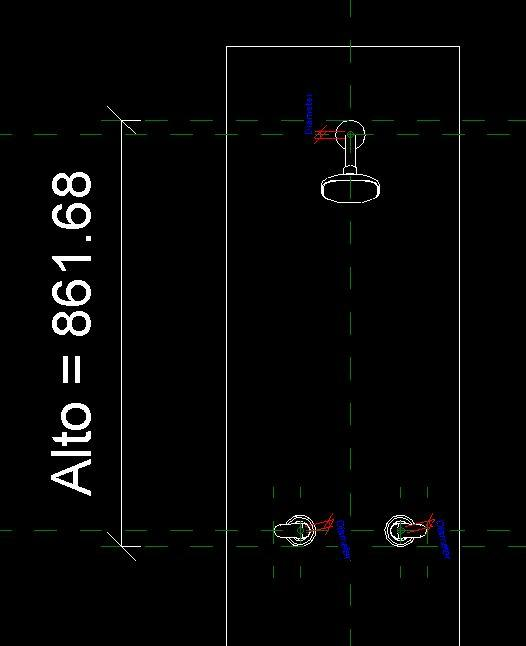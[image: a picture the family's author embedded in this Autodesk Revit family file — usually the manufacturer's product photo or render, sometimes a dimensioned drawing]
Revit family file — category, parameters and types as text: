
# Revit family: CA4005551_Ducha 8 pulgadas Cascade Palanca
name_source: partatom
category: Plumbing Fixtures
units: mm (PartAtom-declared; Revit-internal decimal feet)

## family parameters
Always vertical = Yes
Cut with Voids When Loaded = No
Host = Wall
OmniClass Number = 23.45.05.14.17
OmniClass Title = Showers
Part Type = Normal
Room Calculation Point = No
Round Connector Dimension = Use Diameter
Shared = No

## types (1)
- Type 1
    Alto = 861.68 mm  [stored 2.82703 ft]
    Altura ducha = 2000 mm  [stored 6.56168 ft]
    Altura mezclador = 1200 mm
    Ancho = 310 mm
    Capacidad de flujo = 80 psi: 9,5 L/min
    Fabricante = Corona
    Garantía = 30 años
    Material = Corona_Acero
    Peso neto = 1.040 g. - 2,29 lb
    Presion maxima = 125 psi (862 Kpa)
    Presion minima = 20 psi (138 Kpa)
    Profundidad = 363 mm
    Referencia = CA4005551
    Temperatura de uso = 5˚C a 71˚C
    URL = https://corona.co

note: [stored X ft] marks values corroborated as IEEE doubles in the binary element streams (Revit-internal decimal feet)

## geometry (parser evidence)
native form markers: Sweep x8
no freeform markers — native parametric forms only
